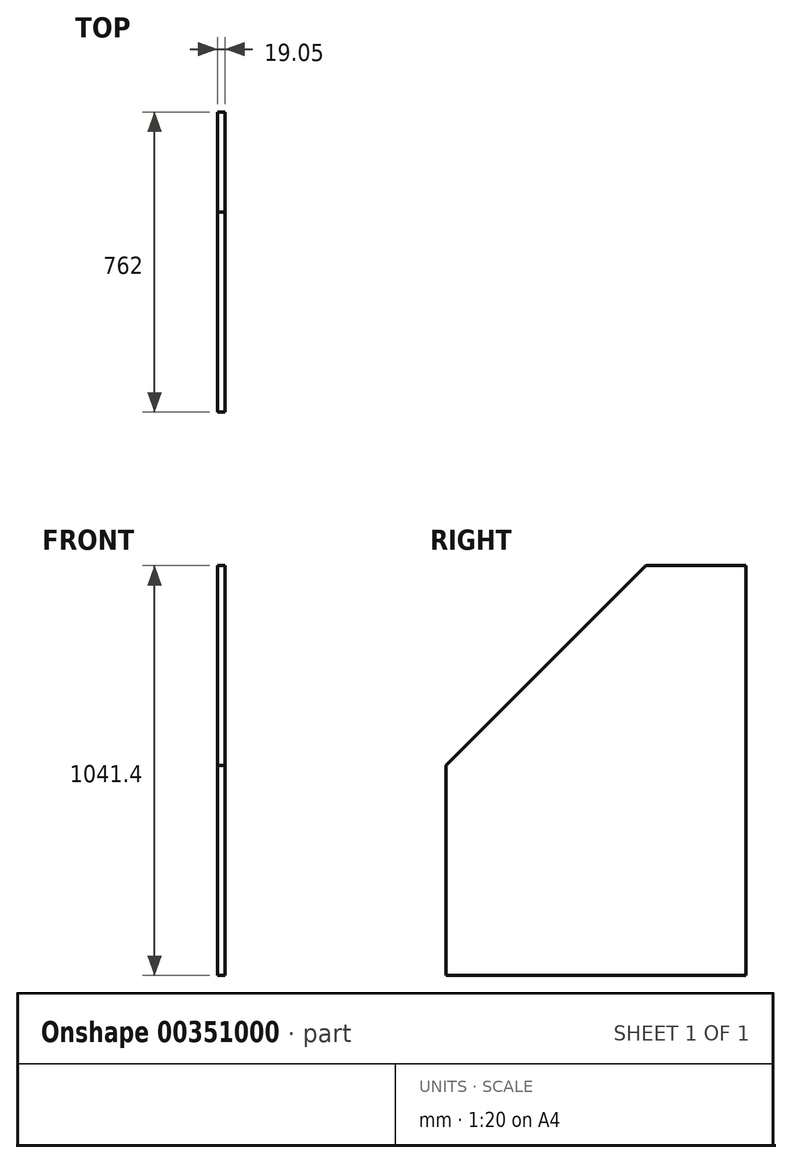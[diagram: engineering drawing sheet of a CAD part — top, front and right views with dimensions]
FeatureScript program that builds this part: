
annotation { "Feature Type Name" : "Feature", "Feature Type Description" : "" }
export const myFeature = defineFeature(function(context is Context, id is Id, definition is map)
    precondition{}
    {
        {
            var Q0;
            Q0=qCreatedBy(makeId("Right.planeOp"),FACE);
            var sketch = newSketch(context, id + "F0", { "sketchPlane" : qUnion([Q0])});
            skLineSegment(sketch, "E0", {"start": v(-374.84, -245.23) * mm, "end": v(-374.84, 288.17) * mm});
            skLineSegment(sketch, "E1", {"start": v(-374.84, -245.23) * mm, "end": v(387.16, -245.23) * mm});
            skLineSegment(sketch, "E2", {"start": v(-374.84, 288.17) * mm, "end": v(133.16, 796.17) * mm});
            skLineSegment(sketch, "E3", {"start": v(387.16, -245.23) * mm, "end": v(387.16, 796.17) * mm});
            skLineSegment(sketch, "E4", {"start": v(133.16, 796.17) * mm, "end": v(387.16, 796.17) * mm});
            skSolve(sketch);
        }
        {
            var Q0;
            Q0 = qSketchRegion(id + "F0", true);
            extrude(context, id + "F1", {"entities" : qUnion([Q0]), "depth" : 19.05 * mm});
        }
    });
